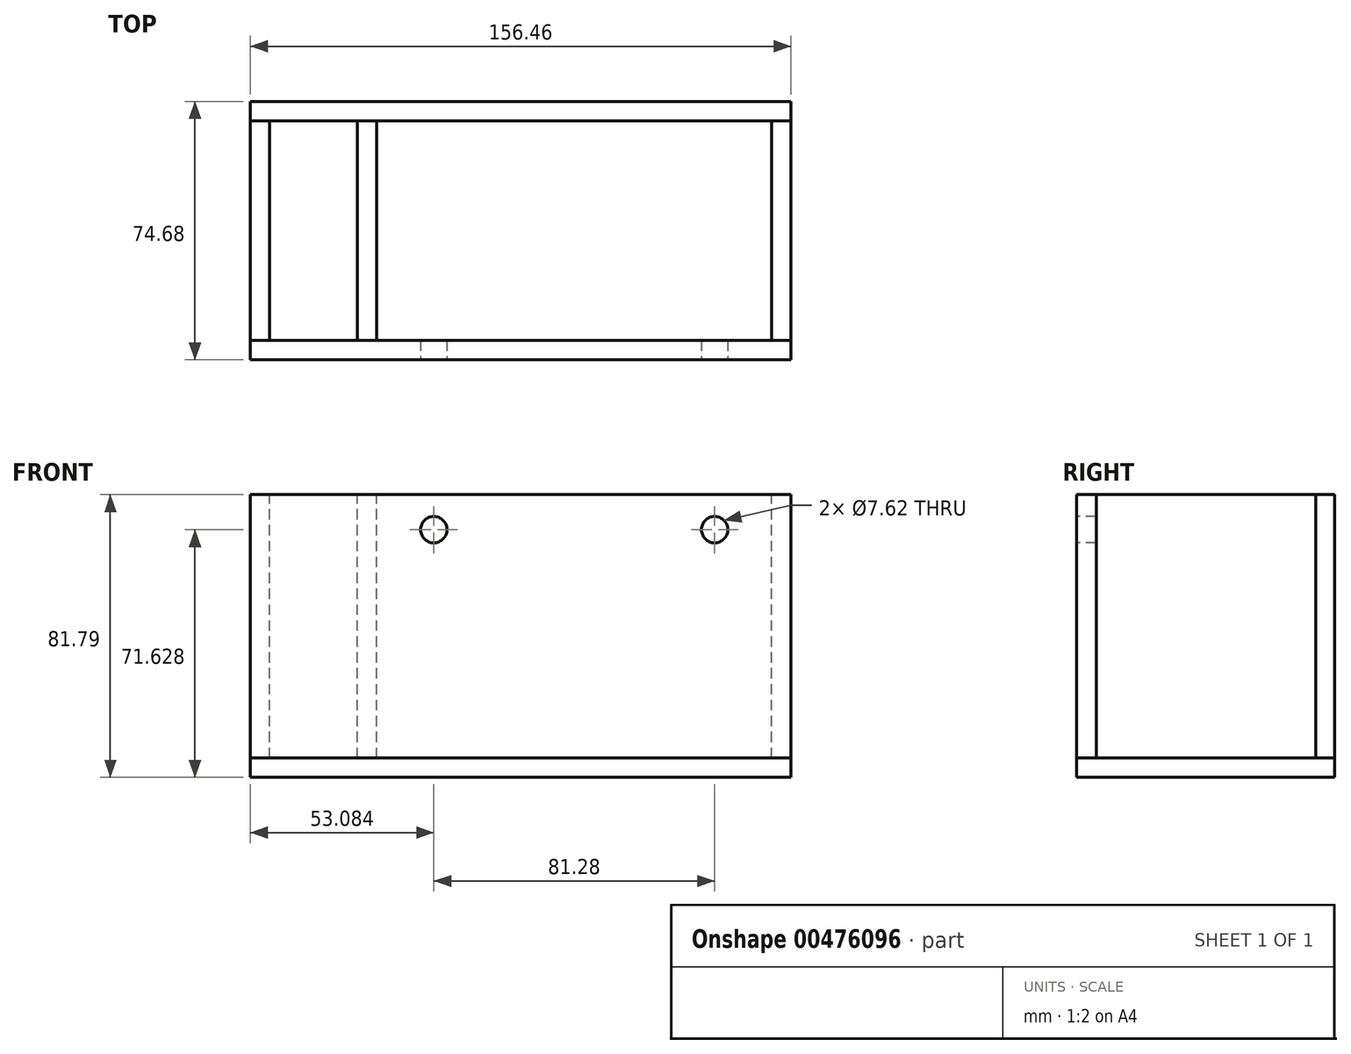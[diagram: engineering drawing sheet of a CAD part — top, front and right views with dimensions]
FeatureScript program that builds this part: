
annotation { "Feature Type Name" : "Feature", "Feature Type Description" : "" }
export const myFeature = defineFeature(function(context is Context, id is Id, definition is map)
    precondition{}
    {
        {
            var Q0;
            Q0=qCreatedBy(makeId("Top.planeOp"),FACE);
            var sketch = newSketch(context, id + "F0", { "sketchPlane" : qUnion([Q0])});
            skLineSegment(sketch, "E0.bottom", {"start": v(78.23, -37.34) * mm, "end": v(-78.23, -37.34) * mm});
            skLineSegment(sketch, "E0.top", {"start": v(78.23, 37.34) * mm, "end": v(-78.23, 37.34) * mm});
            skLineSegment(sketch, "E0.left", {"start": v(78.23, -37.34) * mm, "end": v(78.23, 37.34) * mm});
            skLineSegment(sketch, "E0.right", {"start": v(-78.23, -37.34) * mm, "end": v(-78.23, 37.34) * mm});
            skPoint(sketch, "E0.middle", {"position": v(0, 0) * mm});
            skSolve(sketch);
        }
        {
            var Q0;
            Q0 = qSketchRegion(id + "F0", true);
            extrude(context, id + "F1", {"entities" : qUnion([Q0]), "depth" : 5.6 * mm, "offsetDistance" : 25.4 * mm});
        }
        {
            var Q0;
            Q0=makeQuery(id+"F1.opExtrude","CAP_FACE",FACE,{"disambiguationData":[OSD([sQuery(id+"F0.wireOp",EDGE,"E0.bottom"),sQuery(id+"F0.wireOp",EDGE,"E0.top"),sQuery(id+"F0.wireOp",EDGE,"E0.left"),sQuery(id+"F0.wireOp",EDGE,"E0.right")])],"isStart":false});
            var sketch = newSketch(context, id + "F2", { "sketchPlane" : qUnion([Q0])});
            skLineSegment(sketch, "E1", {"start": v(-78.23, 31.75) * mm, "end": v(78.23, 31.75) * mm});
            skSolve(sketch);
        }
        {
            var Q0;
            {var subQ0=sQuery(id+"F2.wireOp",EDGE,"E1");Q0=makeQuery(id+"F2.imprint","IMPRINT",FACE,{"disambiguationData":[TD([[makeQuery(id+"F2.imprint","IMPRINT",EDGE,{"derivedFrom":subQ0}),1.0]])]});}
            extrude(context, id + "F3", {"entities" : qUnion([Q0]), "depth" : 76.2 * mm, "offsetDistance" : 25.4 * mm});
        }
        {
            var Q0;
            Q0=makeQuery(id+"F1.opExtrude","CAP_FACE",FACE,{"disambiguationData":[OSD([sQuery(id+"F0.wireOp",EDGE,"E0.bottom"),sQuery(id+"F0.wireOp",EDGE,"E0.top"),sQuery(id+"F0.wireOp",EDGE,"E0.left"),sQuery(id+"F0.wireOp",EDGE,"E0.right")])],"isStart":false});
            var sketch = newSketch(context, id + "F4", { "sketchPlane" : qUnion([Q0])});
            skLineSegment(sketch, "E2", {"start": v(-78.23, -31.75) * mm, "end": v(78.23, -31.75) * mm});
            skSolve(sketch);
        }
        {
            var Q0;
            {var subQ0=sQuery(id+"F4.wireOp",EDGE,"E2");Q0=makeQuery(id+"F4.imprint","IMPRINT",FACE,{"disambiguationData":[TD([[makeQuery(id+"F4.imprint","IMPRINT",EDGE,{"derivedFrom":subQ0}),-1.0]])]});}
            extrude(context, id + "F5", {"entities" : qUnion([Q0]), "depth" : 76.2 * mm, "offsetDistance" : 25.4 * mm});
        }
        {
            var Q0;
            Q0=makeQuery(id+"F3.opExtrude","SWEPT_FACE",FACE,{"disambiguationData":[OSD([sQuery(id+"F2.wireOp",EDGE,"E1")])]});
            var sketch = newSketch(context, id + "F6", { "sketchPlane" : qUnion([Q0])});
            skLineSegment(sketch, "E3", {"start": v(-72.64, 81.79) * mm, "end": v(-72.64, 5.59) * mm});
            skSolve(sketch);
        }
        {
            var Q0;
            {var subQ0=sQuery(id+"F6.wireOp",EDGE,"E3");Q0=makeQuery(id+"F6.imprint","IMPRINT",FACE,{"disambiguationData":[TD([[makeQuery(id+"F6.imprint","IMPRINT",EDGE,{"derivedFrom":subQ0}),-1.0]])]});}
            extrude(context, id + "F7", {"entities" : qUnion([Q0]), "endBound" : BoundingType.UP_TO_NEXT, "depth" : 25.4 * mm, "offsetDistance" : 25.4 * mm});
        }
        {
            var Q0;
            Q0=makeQuery(id+"F3.opExtrude","SWEPT_FACE",FACE,{"disambiguationData":[OSD([sQuery(id+"F2.wireOp",EDGE,"E1")])]});
            var sketch = newSketch(context, id + "F8", { "sketchPlane" : qUnion([Q0])});
            skLineSegment(sketch, "E4", {"start": v(72.64, 81.79) * mm, "end": v(72.64, 5.59) * mm});
            skSolve(sketch);
        }
        {
            var Q0;
            {var subQ0=sQuery(id+"F8.wireOp",EDGE,"E4");Q0=makeQuery(id+"F8.imprint","IMPRINT",FACE,{"disambiguationData":[TD([[makeQuery(id+"F8.imprint","IMPRINT",EDGE,{"derivedFrom":subQ0}),1.0]])]});}
            extrude(context, id + "F9", {"entities" : qUnion([Q0]), "endBound" : BoundingType.UP_TO_NEXT, "depth" : 25.4 * mm, "offsetDistance" : 25.4 * mm});
        }
        {
            var Q0;
            Q0=makeQuery(id+"F3.opExtrude","SWEPT_FACE",FACE,{"disambiguationData":[OSD([sQuery(id+"F2.wireOp",EDGE,"E1")])]});
            var sketch = newSketch(context, id + "F10", { "sketchPlane" : qUnion([Q0])});
            skLineSegment(sketch, "E5", {"start": v(-47.24, 81.79) * mm, "end": v(-47.24, 5.59) * mm});
            skLineSegment(sketch, "E6", {"start": v(-41.66, 81.79) * mm, "end": v(-41.66, 5.59) * mm});
            skSolve(sketch);
        }
        {
            var Q0;
            {var subQ0=sQuery(id+"F10.wireOp",EDGE,"E5");Q0=makeQuery(id+"F10.imprint","IMPRINT",FACE,{"disambiguationData":[TD([[makeQuery(id+"F10.imprint","IMPRINT",EDGE,{"derivedFrom":subQ0}),1.0]])]});}
            extrude(context, id + "F11", {"entities" : qUnion([Q0]), "endBound" : BoundingType.UP_TO_NEXT, "depth" : 25.4 * mm, "offsetDistance" : 25.4 * mm});
        }
        {
            var Q0;
            Q0=makeQuery(id+"F5.opExtrude","SWEPT_FACE",FACE,{"disambiguationData":[OSD([sQuery(id+"F0.wireOp",EDGE,"E0.bottom")])]});
            var sketch = newSketch(context, id + "F12", { "sketchPlane" : qUnion([Q0])});
            skCircle(sketch, "E7", {"center": v(-25.15, 71.63) * mm, "radius": 3.81 * mm});
            skCircle(sketch, "E8", {"center": v(56.13, 71.63) * mm, "radius": 3.81 * mm});
            skSolve(sketch);
        }
        {
            var Q0;
            Q0 = qSketchRegion(id + "F12", true);
            var Q1;
            Q1=makeQuery(id+"F5.opExtrude","SWEPT_FACE",FACE,{"disambiguationData":[OSD([sQuery(id+"F4.wireOp",EDGE,"E2")])]});
            extrude(context, id + "F13", {"entities" : qUnion([Q0]), "operationType" : NewBodyOperationType.REMOVE, "endBound" : BoundingType.UP_TO_SURFACE, "oppositeDirection" : true, "depth" : 25.4 * mm, "endBoundEntityFace" : qUnion([Q1]), "offsetDistance" : 25.4 * mm});
        }
    });
